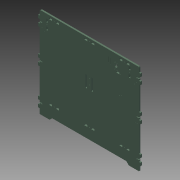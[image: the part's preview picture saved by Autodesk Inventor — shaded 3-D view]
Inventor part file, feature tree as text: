
AUTODESK INVENTOR PART (.ipt)
format: ipt  version: 2013 (Build 170138000, 138)  size: 445,440 bytes
history: native  units: mm
features: extrude x2, sketch x2
ambient origin geometry x8: Origin, YZ Plane, XZ Plane, XY Plane, X Axis, Y Axis, Z Axis, Center Point
bodies: Solid1 (feature_tree)
feature tree (4):
  extrude  "Extrusion1"  Depth=48.498637mm
  extrude  "Extrusion2"  Depth=395.2mm
  sketch  "Sketch1"  dims[d0=5.992494mm d1=48.498637mm]
  sketch  "Sketch2"  dims[d2=359.4mm d3=395.2mm d4=5.0mm d5=6.0mm d6=0.0mm d7=38.5mm d8=12.4mm d9=6.1mm d10=11.8mm d11=0.3mm d12=6.0mm d13=3.0mm d14=7.0mm d15=1.8mm d16=1.8mm d17=1.25mm d18=1.25mm d19=6.1mm d20=12.4mm d21=135.0mm d22=6.1mm d23=12.4mm d24=3.0mm d25=6.1mm d26=12.4mm d31=144.4mm d32=6.1mm d33=12.4mm d34=3.0mm d35=6.1mm d36=12.4mm d39=11.2mm d41=140.0mm d42=140.0mm d43=6.4mm d44=3.2mm d45=3.0mm d46=12.0mm d47=7.8mm d48=7.8mm d49=12.0mm d50=7.8mm d51=7.8mm d52=12.0mm d53=12.0mm d54=7.8mm d55=12.0mm d56=7.8mm d57=12.0mm d58=53.2mm d59=3.2mm d61=6.4mm d62=6.4mm d63=11.9mm d64=4.0mm d65=61.195099mm d66=74.457008mm d67=3.2mm d68=8.0mm d69=24.0mm d70=30.077799mm d71=87.664143mm d72=4.0mm d73=12.0mm d74=12.0mm d75=20.0mm d76=9.5mm d77=26.0mm d78=111.7mm d79=1.25mm d80=46.514563mm d81=6.4mm d82=6.4mm d83=21.5mm d84=138.75mm d85=197.6mm d86=8.8mm d87=8.8mm d88=7.75mm d89=9.0mm d90=9.0mm d91=9.0mm d92=58.0mm d93=9.0mm d94=9.0mm d95=40.0mm d96=40.0mm d97=10.0mm d98=135.0deg d99=197.6mm d100=10.6mm d101=1.8mm d102=1.8mm d103=6.0mm d104=8.0mm d105=7.0mm d106=160.937332mm d107=3.0mm d109=3.0mm d110=6.1mm d111=6.1mm d112=12.0mm d113=12.0mm d114=15.0mm d115=7.5mm d116=3.05mm d117=3.05mm d118=26.5mm d119=3.1mm d120=34.0mm d121=10.0mm d122=0.0mm]
